# Revit family: Door-Slider-Pocket-Fleetwood-3070-PXXX
name_source: partatom
category: Doors
revit_build: Autodesk Revit Architecture 2013 (Build: 20120221_2030(x64)
units: mm (PartAtom-declared; Revit-internal decimal feet)

## types (1)
- Archetype Hardware - 3.5" Sightline Extender
    Actuator_Height = 53.75 "
    Analytic Construction = <None>
    Configuration = PXXX
    Custom_CL_1 = 0 "
    Custom_CL_2 = 0 "
    Custom_Centerlines = No
    Daylight_Opening = 96 "
    Equal Glass Sizes = Yes
    Equal_Centerlines = No
    Exterior Wrap Overhang = 0.5 "
    Frame_&_Panel = Aluminum, Anodized Clear
    Function = Exterior
    Glazing = Glass
    Hardware = Stainless Steel, Brushed
    Height = 96 "
    Interior Wrap Overhang = 0.375 "
    Manufacturer = Fleetwood Windows and Doors
    Model = 3070
    Panel_Width_1 = 33.8465 "
    Panel_Width_2 = 31.9515 "
    Panel_Width_3 = 35.4515 "
    Pocket_Width = 37.75 "
    Rough Height = 96.25 "
    Rough Width = 134 "
    Shim_Space = 0.25 "
    Thickness = 5.724 "
    URL = www.fleetwoodusa.com
    Wall Closure = By host
    Width = 133.5 "

## geometry (parser evidence)
native form markers: Blend x12, Sweep x14
no freeform markers — native parametric forms only
